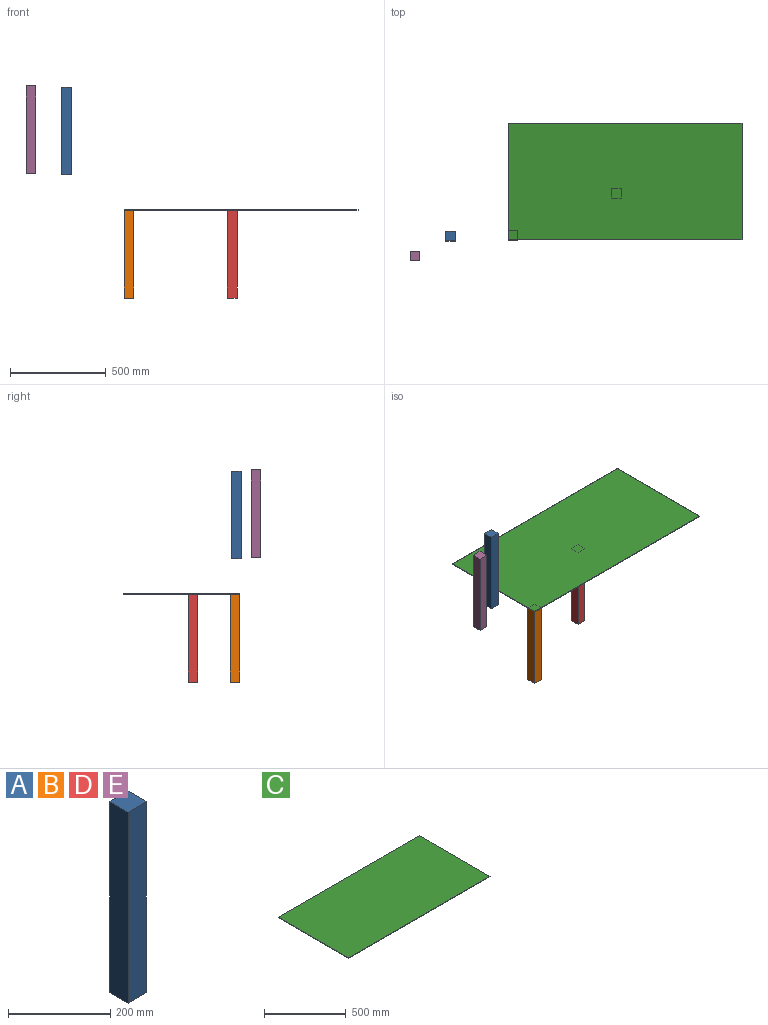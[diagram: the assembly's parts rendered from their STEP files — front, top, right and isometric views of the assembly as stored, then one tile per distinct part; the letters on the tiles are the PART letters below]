
ASSEMBLY  parts=5 mates=2
PART A: 6 faces, bbox 50.8x50.8x457.2 mm
  f0: plane 457.2x50.8mm, normal (1,0,0), area 23225.8mm2, adj f1,f3,f4,f5
  f1: plane 457.2x50.8mm, normal (0,1,0), area 23225.8mm2, adj f0,f2,f4,f5
  f2: plane 457.2x50.8mm, normal (-1,0,0), area 23225.8mm2, adj f1,f3,f4,f5
  f3: plane 457.2x50.8mm, normal (0,-1,0), area 23225.8mm2, adj f0,f2,f4,f5
  f4: plane 50.8x50.8mm, normal (0,0,1), area 2580.6mm2, adj f0,f1,f2,f3
  f5: plane 50.8x50.8mm, normal (0,0,-1), area 2580.6mm2, adj f0,f1,f2,f3
PART B: same geometry as A
PART C: 6 faces, bbox 1219.2x609.6x3.2 mm
  f0: plane 609.6x3.18mm, normal (1,0,0), area 1935.5mm2, adj f1,f3,f4,f5
  f1: plane 1219.2x3.18mm, normal (0,1,0), area 3871mm2, adj f0,f2,f4,f5
  f2: plane 609.6x3.18mm, normal (-1,0,0), area 1935.5mm2, adj f1,f3,f4,f5
  f3: plane 1219.2x3.18mm, normal (0,-1,0), area 3871mm2, adj f0,f2,f4,f5
  f4: plane 1219.2x609.6mm, normal (0,0,1), area 743224.3mm2, adj f0,f1,f2,f3
  f5: plane 1219.2x609.6mm, normal (0,0,-1), area 743224.3mm2, adj f0,f1,f2,f3
PART D: same geometry as A
PART E: same geometry as A
PLACE A t=(-909.95,-285.61,182.44)mm
PLACE B t=(-584.2,-279.4,-460.38)mm
PLACE C t=(0,0,-3.18)mm
PLACE D t=(-45.57,-60.59,-460.38)mm
PLACE E t=(-1096.28,-388.95,188.8)mm
MATE fastened C.f5 <-> B.f4  axis (0,0,-1) through (-609.6,-304.8,-3.18)mm
MATE planar D.f4 <-> C.f5  axis (0,0,1) through (-45.57,-60.59,-3.17)mm
